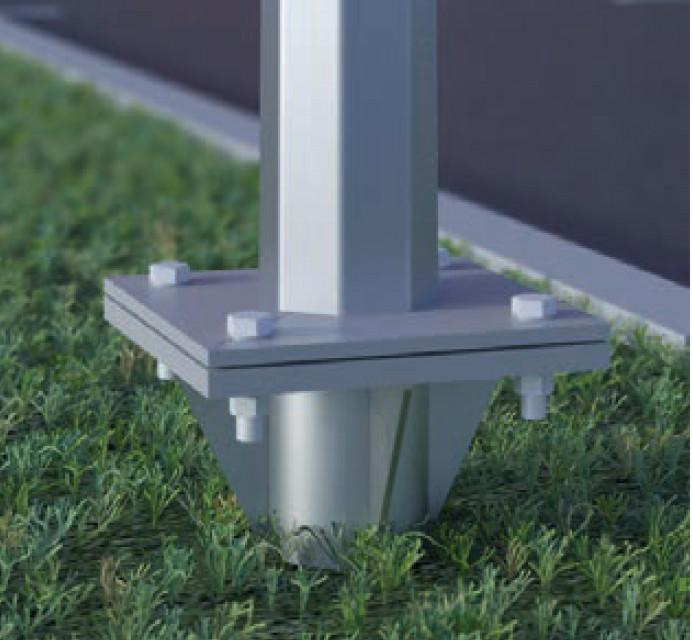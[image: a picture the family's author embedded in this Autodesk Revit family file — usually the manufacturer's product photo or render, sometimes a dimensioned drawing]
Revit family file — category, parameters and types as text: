
# Revit family: Световой боллард Акцент
name_source: partatom
category: Осветительные приборы
revit_build: Autodesk Revit 2018 (Build: 20180423_1000(x64)
units: mm (PartAtom-declared; Revit-internal decimal feet)

## family parameters
Источник света = Нет
Общий = Нет
Основа = Грань
При загрузке вырезать с полостями = Да
Размер круглого соединителя = Использовать диаметр
Тип детали = Нормальный
Точка расчета площади = Нет

## types (2) — shared parameters
ADSK_Версия Revit = 2018
ADSK_Версия семейства = 1.01
ADSK_Единица измерения = шт.
ADSK_Завод-изготовитель = ООО «ОПОРА ИНЖИНИРИНГ»
ADSK_Количество = 1
ADSK_Материал = Сталь
ADSK_Обозначение = ГОСТ Р 1.4 – 2004, ГОСТ Р 1.5 – 2004, ГОСТ 16350-80, ГОСТ Р 1.12 – 2004, ГОСТ 8732-78, ГОСТ 10704-81, ГОСТ 11533-75, ГОСТ 27772-88*, ГОСТ 14771 -76, ГОСТ 23518-79, ГОСТ 14776-79*, ГОСТ 9.032-74* ЕСЗК, ГОСТ 9.307-89 ЕСЗК, ГОСТ 23118-99, ГОСТ 24297-87, ГОСТ 15.309-98, ГОСТ Р 15.201-2000
ADSK_Размер_Длина = 100 мм
ADSK_Размер_Ширина = 160 мм
H = 800 мм
URL = https://opora-e.com
h1 = 403 мм
А = 320 мм
Вид опоры = К
Группа модели = Осветительный комплект
Изготовитель = ООО «ОПОРА ИНЖИНИРИНГ»
Класс Защиты = 1
Класс защиты от поражения электрическим током = I
Климатическая зона = III
Климатическое исполнение = У1
Наличие лючка = Нет
Наличие цоколя = Нет
Область использования = Садово-парковое освещение
Описание = Боллард с подсветкой
Отметка по умолчанию = 1219 мм
Покрытие = Цинк, порошковая покраска
Провод питания = Подземный
Сайт изготовителя = https://www.opora-e.com
Серия = Осветительный комплект
Способ установки = Ф
Срок службы = 25 лет
Телефон изготовителя = +7 (495) 785-50-28
Тип монтажной поверхности = грунт
Тип опоры = Несиловая
Тип продукции = Осветительный комплект
Характеристика заземления = Болт заземления М10
zero-valued in all types: ADSK_Масса, Максимальное горизонтальное усилие, Максимальный вес оборудования

## per-type parameters (varying)
| type | ADSK_Код изделия | ADSK_Наименование краткое | Светильник |
| Световой боллард Акцент LED-20/727/YW360F в комплекте с анкерной закладной | 19717 | Акцент LED-20/727/YW360F | GALAD Акцент LED под анкер : Световой боллард "Акцент" LED-20/727/YW360F в комплекте с анкерной закладной |
| Световой боллард Акцент LED-15/727/YW360F  в комплекте с анкерной закладной | 19716 | Акцент LED-15/727/YW360F | GALAD Акцент LED под анкер : Световой боллард "Акцент" LED-15/727/YW360F  в комплекте с анкерной закладной |

note: column(s) folded — value = type name in every type: ADSK_Марка, ADSK_Наименование
